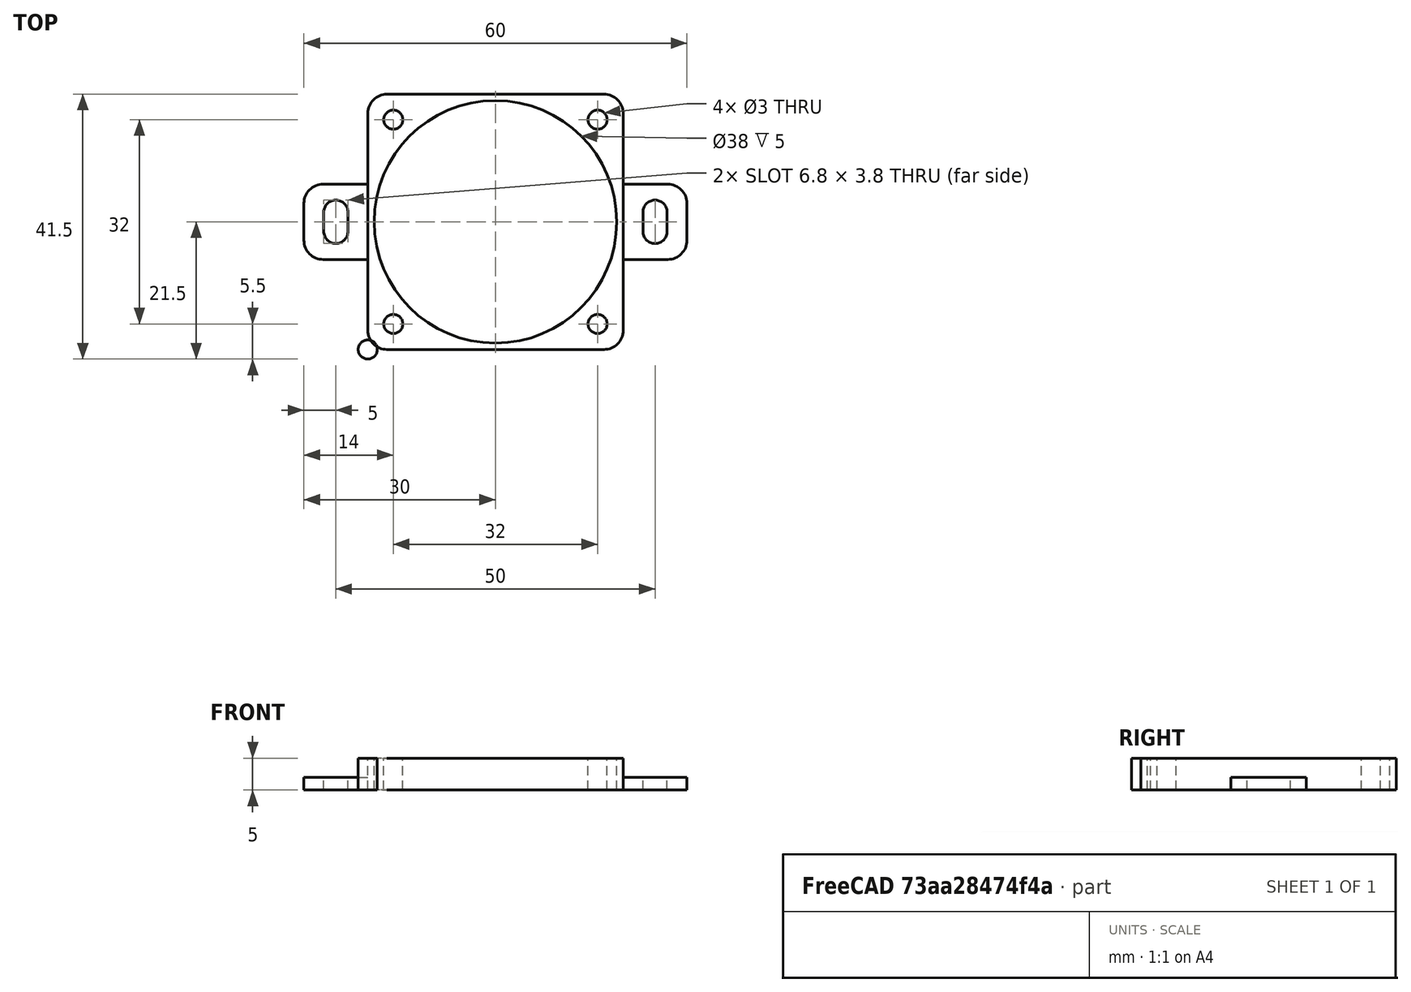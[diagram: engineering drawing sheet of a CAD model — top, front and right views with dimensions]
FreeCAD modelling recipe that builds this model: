
FCSTD DOCUMENT  (FreeCAD 0.19R23578 (Git))
Label: fan_afb0412_plate
License: All rights reserved
LicenseURL: http://en.wikipedia.org/wiki/All_rights_reserved
objects: Part::Cylinder×2, Part::MultiFuse×2, Part::Box×1, Spreadsheet::Sheet×1, Part::FeaturePython×1, Part::Feature×1, Part::Fillet×1, Part::Cut×1
note: 8 computed .brp shape members not serialized (recipe doc carries the construction recipe); baked Part::Feature solids carry a one-line shape summary decoded from their .brp

FEATURE [Part::Box] Box  label="plate cube"
  AttacherType = Attacher::AttachEngine3D
  Height = 5
  Length = 40
  Width = 40
  expr: Length = <<p>>.side_size
  expr: Width = <<p>>.side_size
  expr: Height = <<p>>.under_z
FEATURE [Spreadsheet::Sheet] Spreadsheet  label="p"
  cells = A1=bolt_hole_dist; B1(bolt_hole_dist)==32mm; A2=bolt_hole_r; B2(bolt_hole_r)==1.5mm; A3=centre_hole_r; B3(centre_hole_r)==19mm; A4=under_z; B4(under_z)==5mm; A5=side_size; B5(side_size)==40mm
FEATURE [Part::Cylinder] Cylinder  label="centre hole"
  Angle = 360
  AttacherType = Attacher::AttachEngine3D
  Height = 5
  Placement = pos=(20,20,0) rot=(0,0,1;0rad)
  Radius = 19
  expr: .Placement.Base.y = <<p>>.side_size / 2
  expr: .Placement.Base.x = <<p>>.side_size / 2
  expr: Height = <<p>>.under_z
  expr: Radius = <<p>>.centre_hole_r
FEATURE [Part::Cylinder] Cylinder001  label="bolt_hole"
  Angle = 360
  AttacherType = Attacher::AttachEngine3D
  Height = 5
  Radius = 1.5
  expr: Height = <<p>>.under_z
  expr: Radius = <<p>>.bolt_hole_r
FEATURE [Part::FeaturePython] Array  label="bolt hole array"  # Draft array (typed FeaturePython)
  Angle = 360
  ArrayType = 0
  Axis = (0,0,1)
  Base = -> Cylinder001
  Center = (0,0,0)
  Count = 4
  ExpandArray = false
  Fuse = false
  IntervalAxis = (0,0,0)
  IntervalX = (32,0,0)
  IntervalY = (0,32,0)
  IntervalZ = (0,0,100)
  NumberCircles = 3
  NumberPolar = 5
  NumberX = 2
  NumberY = 2
  NumberZ = 1
  Placement = pos=(4,4,0) rot=(0,0,1;0rad)
  PlacementList = 4 placements: [(0,0,0),(0,32,0),(32,0,0),(32,32,0)]
  RadialDistance = 50
  ScaleList = (4) [(1,1,1),(1,1,1),(1,1,1),(1,1,1)]
  Symmetry = 1
  TangentialDistance = 25
  expr: .Placement.Base.y = (<<p>>.side_size - <<p>>.bolt_hole_dist) / 2
  expr: .Placement.Base.x = (<<p>>.side_size - <<p>>.bolt_hole_dist) / 2
  expr: .IntervalY.y = <<p>>.bolt_hole_dist
  expr: .IntervalX.x = <<p>>.bolt_hole_dist
FEATURE [Part::Feature] Cut003002  label="attach plane x dir002"
  Placement = pos=(-10,14.1,0) rot=(0,0,1;0rad)
  shape: bbox 60 x 11.8 x 2 mm, 18 faces (baked)
FEATURE [Part::Fillet] Fillet  label="plate fillet"
  Base = -> Box
  Edges = 4 edges r=3: [Edge1,Edge3,Edge5,Edge7]
FEATURE [Part::MultiFuse] Fusion  label="body fusion"
  Shapes = -> [Fillet,Cut003002]
FEATURE [Part::MultiFuse] Fusion001  label="extract fusion"
  Shapes = -> [Array,Cylinder]
FEATURE [Part::Cut] Cut  label="body cut"
  Base = -> Fusion
  Tool = -> Fusion001
